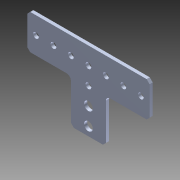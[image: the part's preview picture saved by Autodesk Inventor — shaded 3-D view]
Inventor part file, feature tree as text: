
AUTODESK INVENTOR PART (.ipt)
format: ipt  version: 2015 SP1 (Build 190203100, 203)  size: 152,576 bytes
history: native  units: in
note: dims shown in document units (in); Inventor stores cm internally (conversion verified against a paired STEP export)
features: fillet x1, other x1, extrude x1, imported_body x1, sketch x1, projected_geometry x1
ambient origin geometry x8: Origin, YZ Plane, XZ Plane, XY Plane, X Axis, Y Axis, Z Axis, Center Point
bodies: Body1 (feature_tree)
feature tree (6):
  fillet  "Fillet1"  Radius=0.25in
  other  "VersaFrame Gusset (217-3557)1"
  extrude  "Extrusion1"  Depth=1.0in TaperAngle=0.0deg
  imported_body  "Base1"
  sketch  "Sketch1"  dims[d1=0.25in d2=1.0in d3=0.0in]
  projected_geometry  "Projected Loop1"
